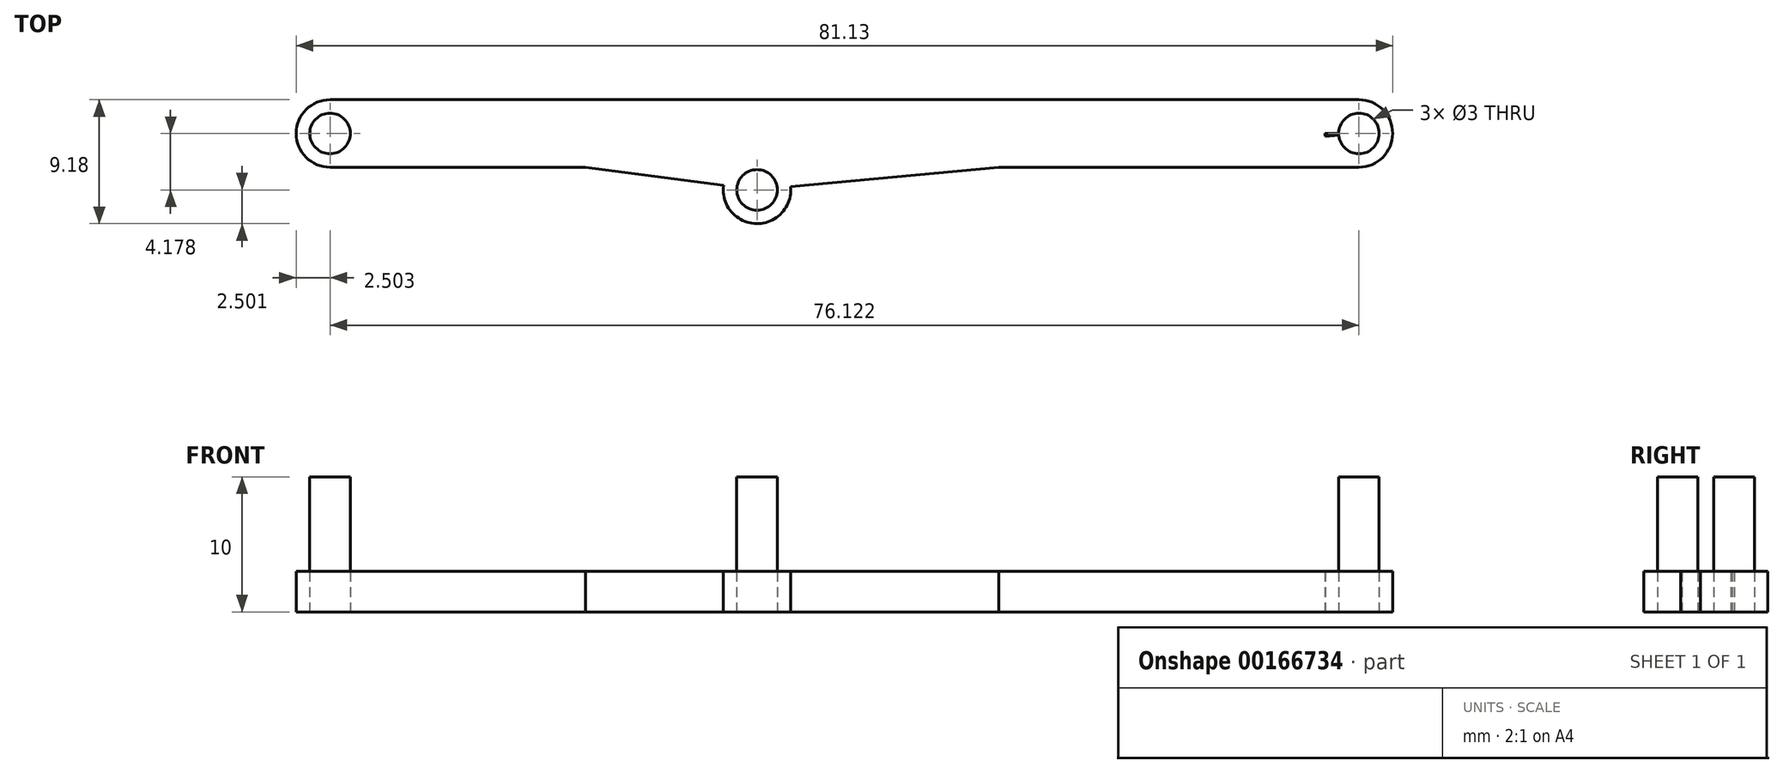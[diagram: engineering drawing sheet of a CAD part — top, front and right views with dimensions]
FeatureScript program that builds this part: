
annotation { "Feature Type Name" : "Feature", "Feature Type Description" : "" }
export const myFeature = defineFeature(function(context is Context, id is Id, definition is map)
    precondition{}
    {
        {
            var Q0;
            Q0=qCreatedBy(makeId("Top.planeOp"),FACE);
            var sketch = newSketch(context, id + "F0", { "sketchPlane" : qUnion([Q0])});
            skLineSegment(sketch, "E0", {"start": v(55.97, 6.13) * mm, "end": v(-20.16, 6.13) * mm});
            skLineSegment(sketch, "E1", {"start": v(-20.16, 6.13) * mm, "end": v(11.44, 1.95) * mm});
            skLineSegment(sketch, "E2", {"start": v(11.44, 1.95) * mm, "end": v(55.97, 6.13) * mm});
            skCircle(sketch, "E3", {"center": v(11.44, 1.95) * mm, "radius": 1.5 * mm});
            skCircle(sketch, "E4", {"center": v(55.97, 6.13) * mm, "radius": 1.5 * mm});
            skCircle(sketch, "E5", {"center": v(-20.16, 6.13) * mm, "radius": 1.5 * mm});
            skCircle(sketch, "E6", {"center": v(11.44, 1.95) * mm, "radius": 2.5 * mm});
            skCircle(sketch, "E7", {"center": v(-20.16, 6.13) * mm, "radius": 2.5 * mm});
            skCircle(sketch, "E8", {"center": v(55.97, 6.13) * mm, "radius": 2.5 * mm});
            skLineSegment(sketch, "E9", {"start": v(-20.16, 3.63) * mm, "end": v(55.97, 3.63) * mm});
            skLineSegment(sketch, "E10", {"start": v(55.97, 8.63) * mm, "end": v(-20.16, 8.63) * mm});
            skSolve(sketch);
        }
        {
            var Q0;
            Q0 = qSketchRegion(id + "F0", true);
            var Q1;
            {var subQ0=sQuery(id+"F0.wireOp",EDGE,"E9");var subQ1=sQuery(id+"F0.wireOp",EDGE,"E6");var subQ2=makeQuery(id+"F0.imprint","INTERSECT",VERTEX,{"disambiguationData":[OD(0.0)],"derivedFrom":[subQ1,subQ0]});Q1=makeQuery(id+"F0.imprint","IMPRINT",FACE,{"disambiguationData":[TD([[makeQuery(id+"F0.imprint","IMPRINT",EDGE,{"disambiguationData":[TD([[subQ2,-1.0]])],"derivedFrom":subQ1}),1.0]])]});}
            var Q2;
            {var subQ0=sQuery(id+"F0.wireOp",EDGE,"E7");var subQ1=sQuery(id+"F0.wireOp",EDGE,"E0");var subQ2=makeQuery(id+"F0.imprint","INTERSECT",VERTEX,{"derivedFrom":[subQ1,subQ0]});Q2=makeQuery(id+"F0.imprint","IMPRINT",FACE,{"disambiguationData":[TD([[makeQuery(id+"F0.imprint","IMPRINT",EDGE,{"disambiguationData":[TD([[subQ2,-1.0]])],"derivedFrom":subQ1}),1.0]])]});}
            var Q3;
            {var subQ0=sQuery(id+"F0.wireOp",EDGE,"E4");var subQ1=sQuery(id+"F0.wireOp",EDGE,"E0");var subQ2=makeQuery(id+"F0.imprint","INTERSECT",VERTEX,{"derivedFrom":[subQ1,subQ0]});Q3=makeQuery(id+"F0.imprint","IMPRINT",FACE,{"disambiguationData":[TD([[makeQuery(id+"F0.imprint","IMPRINT",EDGE,{"disambiguationData":[TD([[subQ2,-1.0]])],"derivedFrom":subQ1}),1.0]])]});}
            extrude(context, id + "F1", {"entities" : qUnion([Q0, Q1, Q2, Q3]), "flatOperationType" : FlatOperationType.REMOVE, "offsetDistance" : 25 * mm, "depth" : 3 * mm, "domain" : OperationDomain.MODEL});
        }
        {
            var Q0;
            {var subQ0=sQuery(id+"F0.wireOp",EDGE,"E1");var subQ1=sQuery(id+"F0.wireOp",EDGE,"E0");var subQ2=makeQuery(id+"F0.imprint","INTERSECT",VERTEX,{"derivedFrom":[subQ1,subQ0]});Q0=makeQuery(id+"F0.imprint","IMPRINT",FACE,{"disambiguationData":[TD([[makeQuery(id+"F0.imprint","IMPRINT",EDGE,{"disambiguationData":[TD([[subQ2,1.0]])],"derivedFrom":subQ1}),-1.0]])]});}
            var Q1;
            {var subQ0=sQuery(id+"F0.wireOp",EDGE,"E1");var subQ1=sQuery(id+"F0.wireOp",EDGE,"E0");var subQ2=makeQuery(id+"F0.imprint","INTERSECT",VERTEX,{"derivedFrom":[subQ1,subQ0]});Q1=makeQuery(id+"F0.imprint","IMPRINT",FACE,{"disambiguationData":[TD([[makeQuery(id+"F0.imprint","IMPRINT",EDGE,{"disambiguationData":[TD([[subQ2,1.0]])],"derivedFrom":subQ1}),1.0]])]});}
            var Q2;
            {var subQ0=sQuery(id+"F0.wireOp",EDGE,"E2");var subQ1=sQuery(id+"F0.wireOp",EDGE,"E1");var subQ2=makeQuery(id+"F0.imprint","INTERSECT",VERTEX,{"derivedFrom":[subQ1,subQ0]});Q2=makeQuery(id+"F0.imprint","IMPRINT",FACE,{"disambiguationData":[TD([[makeQuery(id+"F0.imprint","IMPRINT",EDGE,{"disambiguationData":[TD([[subQ2,1.0]])],"derivedFrom":subQ1}),-1.0]])]});}
            var Q3;
            {var subQ0=sQuery(id+"F0.wireOp",EDGE,"E2");var subQ1=sQuery(id+"F0.wireOp",EDGE,"E1");var subQ2=makeQuery(id+"F0.imprint","INTERSECT",VERTEX,{"derivedFrom":[subQ1,subQ0]});Q3=makeQuery(id+"F0.imprint","IMPRINT",FACE,{"disambiguationData":[TD([[makeQuery(id+"F0.imprint","IMPRINT",EDGE,{"disambiguationData":[TD([[subQ2,1.0]])],"derivedFrom":subQ1}),1.0]])]});}
            var Q4;
            {var subQ0=sQuery(id+"F0.wireOp",EDGE,"E2");var subQ1=sQuery(id+"F0.wireOp",EDGE,"E0");var subQ2=makeQuery(id+"F0.imprint","INTERSECT",VERTEX,{"derivedFrom":[subQ1,subQ0]});Q4=makeQuery(id+"F0.imprint","IMPRINT",FACE,{"disambiguationData":[TD([[makeQuery(id+"F0.imprint","IMPRINT",EDGE,{"disambiguationData":[TD([[subQ2,-1.0]])],"derivedFrom":subQ1}),1.0]])]});}
            var Q5;
            {var subQ0=sQuery(id+"F0.wireOp",EDGE,"E2");var subQ1=sQuery(id+"F0.wireOp",EDGE,"E0");var subQ2=makeQuery(id+"F0.imprint","INTERSECT",VERTEX,{"derivedFrom":[subQ1,subQ0]});Q5=makeQuery(id+"F0.imprint","IMPRINT",FACE,{"disambiguationData":[TD([[makeQuery(id+"F0.imprint","IMPRINT",EDGE,{"disambiguationData":[TD([[subQ2,-1.0]])],"derivedFrom":subQ1}),-1.0]])]});}
            extrude(context, id + "F2", {"entities" : qUnion([Q0, Q1, Q2, Q3, Q4, Q5]), "depth" : 10 * mm});
        }
        {
            var Q0;
            {var subQ5=sQuery(id+"F0.wireOp",EDGE,"E4");var subQ9=sQuery(id+"F0.wireOp",EDGE,"E0");var subQ10=makeQuery(id+"F0.imprint","INTERSECT",VERTEX,{"derivedFrom":[subQ9,subQ5]});Q0=makeQuery(id+"F0.imprint","IMPRINT",FACE,{"disambiguationData":[TD([[makeQuery(id+"F0.imprint","IMPRINT",EDGE,{"disambiguationData":[TD([[subQ10,-1.0]])],"derivedFrom":subQ9}),1.0]])]});}
            extrude(context, id + "F3", {"entities" : qUnion([Q0]), "depth" : 3 * mm});
        }
    });
